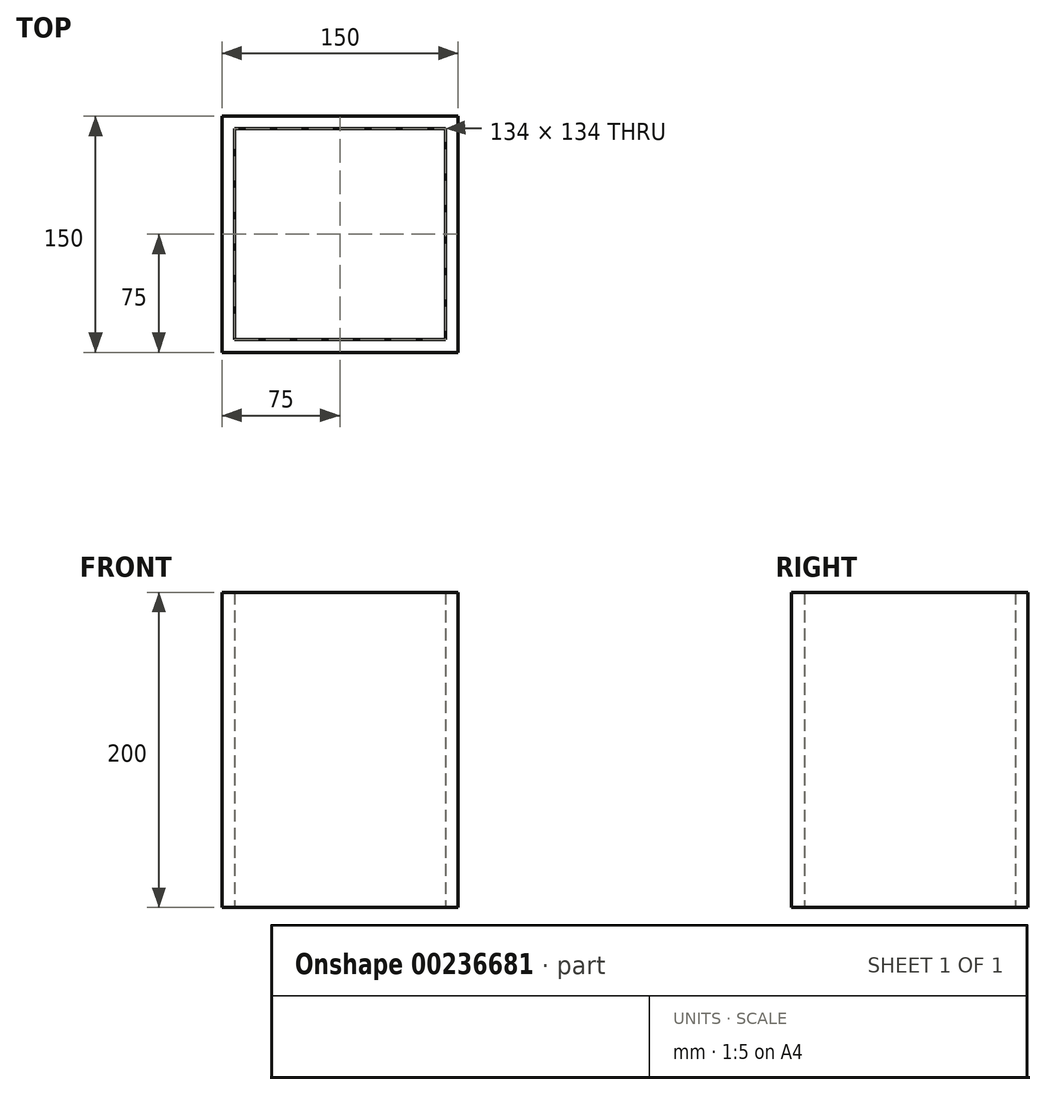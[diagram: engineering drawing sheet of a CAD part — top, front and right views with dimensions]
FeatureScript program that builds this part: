
annotation { "Feature Type Name" : "Feature", "Feature Type Description" : "" }
export const myFeature = defineFeature(function(context is Context, id is Id, definition is map)
    precondition{}
    {
        {
            var Q0;
            Q0=qCreatedBy(makeId("Top.planeOp"), FACE);
            var sketch = newSketch(context, id + "F0", { "sketchPlane" : qUnion([Q0])});
            skLineSegment(sketch, "E0.bottom", {"start": v(75, 75) * mm, "end": v(-75, 75) * mm});
            skLineSegment(sketch, "E0.top", {"start": v(75, -75) * mm, "end": v(-75, -75) * mm});
            skLineSegment(sketch, "E0.left", {"start": v(75, 75) * mm, "end": v(75, -75) * mm});
            skLineSegment(sketch, "E0.right", {"start": v(-75, 75) * mm, "end": v(-75, -75) * mm});
            skPoint(sketch, "E0.middle", {"position": v(0, 0) * mm});
            skLineSegment(sketch, "E1.bottom", {"start": v(67, 67) * mm, "end": v(-67, 67) * mm});
            skLineSegment(sketch, "E1.top", {"start": v(67, -67) * mm, "end": v(-67, -67) * mm});
            skLineSegment(sketch, "E1.left", {"start": v(67, 67) * mm, "end": v(67, -67) * mm});
            skLineSegment(sketch, "E1.right", {"start": v(-67, 67) * mm, "end": v(-67, -67) * mm});
            skSolve(sketch);
        }
        {
            var Q0;
            Q0 = qSketchRegion(id + "F0", true);
            extrude(context, id + "F1", {"entities" : qUnion([Q0]), "depth" : 200 * mm, "offsetDistance" : 25 * mm});
        }
    });
